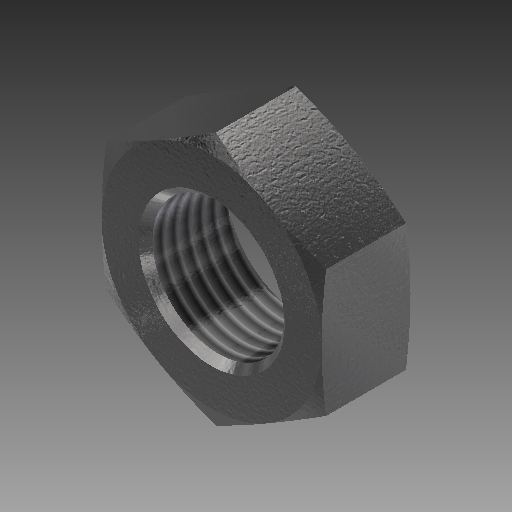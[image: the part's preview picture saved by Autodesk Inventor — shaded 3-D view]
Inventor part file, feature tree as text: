
AUTODESK INVENTOR PART (.ipt)
format: ipt  version: 2017 (Build 210142000, 142)  size: 272,384 bytes
history: native  units: in
note: dims shown in document units (in); Inventor stores cm internally (conversion verified against a paired STEP export)
features: other x70, sketch x3, revolve x2, extrude x1, thread x1
ambient origin geometry x8: Origin, YZ Plane, XZ Plane, XY Plane, X Axis, Y Axis, Z Axis, Center Point
bodies: Solid1 (feature_tree)
feature tree (77):
  sketch  "Sketch_8"  dims[d0=360.0deg d1=0.38in d2=0.0in]
  sketch  "Sketch_10"  dims[d3=360.0deg d4=0.3199in d5=0.0in]
  revolve  "Revolution1"  [1 undecoded]
  extrude  "Extrusion1"  Depth=0.3199in TaperAngle=0.0deg
  revolve  "Revolution2"  [1 undecoded]
  thread  "Thread1"  [1 undecoded]
  other  "NUT_XY"
  other  "NUT_YZ"
  other  "NUT_ZX"
  other  "NUT_X"
  other  "NUT_Y"
  other  "NUT_Z"
  other  "NUT_Center"
  other  "a1_XY"
  other  "a1_YZ"
  other  "a1_ZX"
  other  "a1_X"
  other  "a1_Y"
  other  "a1_Z"
  other  "a1_Center"
  other  "a2_XY"
  other  "a2_YZ"
  other  "a2_ZX"
  other  "a2_X"
  other  "a2_Y"
  other  "a2_Z"
  other  "a2_Center"
  other  "b1_XY"
  other  "b1_YZ"
  other  "b1_ZX"
  other  "b1_X"
  other  "b1_Y"
  other  "b1_Z"
  other  "b1_Center"
  other  "b2_XY"
  other  "b2_YZ"
  other  "b2_ZX"
  other  "b2_X"
  other  "b2_Y"
  other  "b2_Z"
  other  "b2_Center"
  other  "e_XY"
  other  "e_YZ"
  other  "e_ZX"
  other  "e_X"
  other  "e_Y"
  other  "e_Z"
  other  "e_Center"
  other  "ol1_XY"
  other  "ol1_YZ"
  other  "ol1_ZX"
  other  "ol1_X"
  other  "ol1_Y"
  other  "ol1_Z"
  other  "ol1_Center"
  other  "ol2_XY"
  other  "ol2_YZ"
  other  "ol2_ZX"
  other  "ol2_X"
  other  "ol2_Y"
  other  "ol2_Z"
  other  "ol2_Center"
  other  "th1_XY"
  other  "th1_YZ"
  other  "th1_ZX"
  other  "th1_X"
  other  "th1_Y"
  other  "th1_Z"
  other  "th1_Center"
  other  "th2_XY"
  other  "th2_YZ"
  other  "th2_ZX"
  other  "th2_X"
  other  "th2_Y"
  other  "th2_Z"
  other  "th2_Center"
  sketch  "Sketch_11"  dims[d6=0.0in]
note: 3 required parameter values undecoded (feature->parameter linkage not recoverable at this tier; creation-order binding heuristic only, values carry confidence <= 0.55)